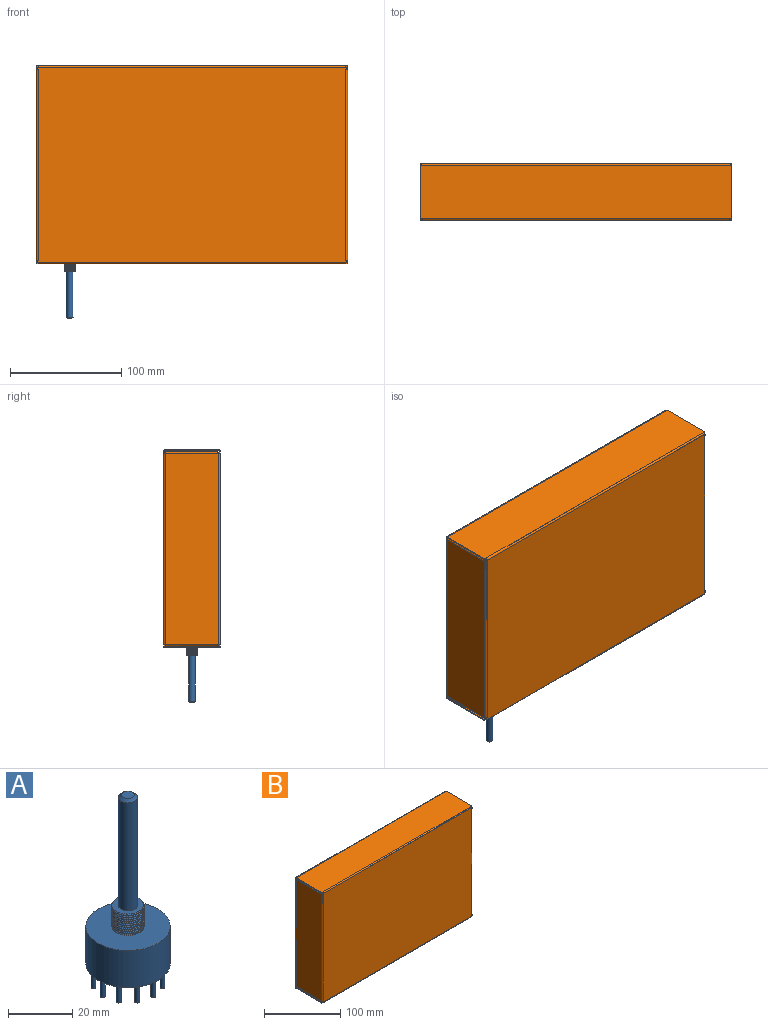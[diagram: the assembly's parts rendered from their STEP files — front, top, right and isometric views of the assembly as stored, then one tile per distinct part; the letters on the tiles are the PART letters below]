
ASSEMBLY  parts=2 mates=1
PART A: 35 faces, bbox 26.4x26.4x71.3 mm
  f0: cylinder r=5mm len=10mm, axis (0,0,-1), area 117.9mm2, adj f1,f2,f3,f4,f8
  f1: plane 10.15x9.87mm, normal (0,0,1), area 47.4mm2, adj f0,f3,f4,f5
  f2: plane 0.4x0.3mm, normal (-0.87,-0.5,0), area 0.1mm2, adj f0,f3,f4
  f3: bspline ~11.55x10mm, area 128mm2, adj f0,f1,f2,f4
  f4: bspline ~11.55x10mm, area 124.5mm2, adj f0,f1,f2,f3
  f5: cylinder r=3mm len=41mm, axis (0,0,-1), area 772.8mm2, adj f1,f7
  f6: plane 4x4mm, normal (0,0,1), area 12.6mm2, adj f7
  f7: cone r=2mm half-angle=45deg, axis (0,0,-1), area 22.2mm2, adj f5,f6
  f8: plane 26.2x26.2mm, normal (0,0,1), area 460.6mm2, adj f0,f9
  f9: cylinder r=13.1mm len=26.2mm, axis (0,0,1), area 1160.6mm2, adj f8,f10
  f10: plane 26.2x26.2mm, normal (0,0,-1), area 517.9mm2, adj f9,f11,f13,f15,f17,f19,f21,f23
  f11: cylinder r=0.75mm len=7mm, axis (0,0,1), area 33mm2, adj f10,f12
  f12: plane 1.5x1.5mm, normal (0,0,-1), area 1.8mm2, adj f11
  f13: cylinder r=0.75mm len=7mm, axis (0,0,1), area 33mm2, adj f10,f14
  f14: plane 1.5x1.5mm, normal (0,0,-1), area 1.8mm2, adj f13
  f15: cylinder r=0.75mm len=7mm, axis (0,0,1), area 33mm2, adj f10,f16
  f16: plane 1.5x1.5mm, normal (0,0,-1), area 1.8mm2, adj f15
  f17: cylinder r=0.75mm len=7mm, axis (0,0,1), area 33mm2, adj f10,f18
  f18: plane 1.5x1.5mm, normal (0,0,-1), area 1.8mm2, adj f17
  f19: cylinder r=0.75mm len=7mm, axis (0,0,1), area 33mm2, adj f10,f20
  f20: plane 1.5x1.5mm, normal (0,0,-1), area 1.8mm2, adj f19
  f21: cylinder r=0.75mm len=7mm, axis (0,0,1), area 33mm2, adj f10,f22
  f22: plane 1.5x1.5mm, normal (0,0,-1), area 1.8mm2, adj f21
  f23: cylinder r=0.75mm len=7mm, axis (0,0,1), area 33mm2, adj f10,f24
  f24: plane 1.5x1.5mm, normal (0,0,-1), area 1.8mm2, adj f23
  f25: cylinder r=0.75mm len=7mm, axis (0,0,1), area 33mm2, adj f10,f26
  f26: plane 1.5x1.5mm, normal (0,0,-1), area 1.8mm2, adj f25
  f27: cylinder r=0.75mm len=7mm, axis (0,0,1), area 33mm2, adj f10,f28
  f28: plane 1.5x1.5mm, normal (0,0,-1), area 1.8mm2, adj f27
  f29: cylinder r=0.75mm len=7mm, axis (0,0,1), area 33mm2, adj f10,f30
  f30: plane 1.5x1.5mm, normal (0,0,-1), area 1.8mm2, adj f29
  f31: cylinder r=0.75mm len=7mm, axis (0,0,1), area 33mm2, adj f10,f32
  f32: plane 1.5x1.5mm, normal (0,0,-1), area 1.8mm2, adj f31
  f33: cylinder r=0.75mm len=7mm, axis (0,0,1), area 33mm2, adj f10,f34
  f34: plane 1.5x1.5mm, normal (0,0,-1), area 1.8mm2, adj f33
PART B: 122 faces, bbox 279.4x50.8x177.8 mm
  f0: bspline ~1.52x1.52mm, area 2.3mm2, adj f1,f49,f53,f100
  f1: cylinder r=1.52mm len=47.75mm, axis (0,1,0), area 112.5mm2, adj f0,f50,f51,f55
  f2: plane 1.52x1.52mm, normal (0,0,-1), area 1.6mm2, adj f3,f4,f39,f43
  f3: cylinder r=0.51mm len=171.7mm, axis (0,0,-1), area 137mm2, adj f2,f45,f54,f57
  f4: cylinder r=1.52mm len=171.7mm, axis (0,0,-1), area 411mm2, adj f2,f46,f54,f55
  f5: cylinder r=1.52mm len=47.75mm, axis (0,-1,0), area 112.5mm2, adj f6,f39,f40,f55
  f6: bspline ~1.52x1.52mm, area 2.3mm2, adj f5,f41,f56,f99
  f7: cylinder r=0.51mm len=47.75mm, axis (0,1,0), area 37.5mm2, adj f8,f35,f36,f62
  f8: bspline ~1.52x1.52mm, area 2.3mm2, adj f7,f33,f58,f98
  f9: plane 8.79x8.79mm, normal (-0.71,0,0.71), area 12.6mm2, adj f11,f44,f45,f46
  f10: plane 8.79x8.79mm, normal (-0.71,0,-0.71), area 12.6mm2, adj f11,f43,f45,f46
  f11: plane 154.94x1.02mm, normal (-1,0,0), area 157.4mm2, adj f9,f10,f45,f46
  f12: plane 1.52x1.02mm, normal (0,-1,0), area 1.5mm2, adj f13,f16,f18,f82
  f13: plane 47.75x1.02mm, normal (-1,0,0), area 48.5mm2, adj f12,f16,f18,f107
  f14: plane 1.52x1.02mm, normal (0,-1,0), area 1.5mm2, adj f16,f17,f18,f79
  f15: plane 29.06x1.02mm, normal (1,0,0), area 29.5mm2, adj f19,f21,f22,f23
  f16: plane 279.4x47.75mm, normal (0,0,-1), area 12457.3mm2, adj f12,f13,f14,f17,f90,f108,f114,f115
  f17: plane 47.75x1.02mm, normal (1,0,0), area 48.5mm2, adj f14,f16,f18,f106
  f18: plane 279.4x47.75mm, normal (0,0,1), area 12457.3mm2, adj f12,f13,f14,f17,f91,f109,f114,f115
  f19: plane 8.38x8.38mm, normal (0.71,0.71,0), area 12mm2, adj f15,f20,f21,f23
  f20: plane 1.93x1.52mm, normal (0,1,0), area 2mm2, adj f19,f21,f23,f93,f94,f95
  f21: plane 46.23x8.79mm, normal (0,0,1), area 332.5mm2, adj f15,f19,f20,f22,f93
  f22: plane 8.79x8.79mm, normal (0.71,-0.71,0), area 12.6mm2, adj f15,f21,f23,f92
  f23: plane 46.23x8.79mm, normal (0,0,-1), area 332.5mm2, adj f15,f19,f20,f22,f94
  f24: plane 1.02x0.41mm, normal (-1,0,0), area 0.4mm2, adj f26,f29,f30,f59
  f25: plane 154.94x1.02mm, normal (1,0,0), area 157.4mm2, adj f26,f27,f29,f30
  f26: plane 8.79x8.79mm, normal (0.71,0,-0.71), area 12.6mm2, adj f24,f25,f29,f30
  f27: plane 8.79x8.79mm, normal (0.71,0,0.71), area 12.6mm2, adj f25,f28,f29,f30
  f28: plane 1.02x0.41mm, normal (-1,0,0), area 0.4mm2, adj f27,f29,f30,f95
  f29: plane 172.52x8.79mm, normal (0,-1,0), area 1425.3mm2, adj f24,f25,f26,f27,f28,f97,f112,f113
  f30: plane 172.52x8.79mm, normal (0,1,0), area 1425.3mm2, adj f24,f25,f26,f27,f28,f96,f112,f113
  f31: plane 8.38x8.38mm, normal (0.71,0.71,0), area 12mm2, adj f32,f34,f35,f36
  f32: plane 29.06x1.02mm, normal (1,0,0), area 29.5mm2, adj f31,f33,f34,f36
  f33: plane 8.79x8.79mm, normal (0.71,-0.71,0), area 12.6mm2, adj f8,f32,f34,f36
  f34: plane 46.23x8.79mm, normal (0,0,-1), area 332.5mm2, adj f31,f32,f33,f35,f98
  f35: plane 1.93x1.52mm, normal (0,1,0), area 2mm2, adj f7,f31,f34,f36,f59,f98
  f36: plane 46.23x8.79mm, normal (0,0,1), area 332.5mm2, adj f7,f31,f32,f33,f35
  f37: plane 29.06x1.02mm, normal (-1,0,0), area 29.5mm2, adj f38,f40,f41,f42
  f38: plane 8.38x8.38mm, normal (-0.71,0.71,0), area 12mm2, adj f37,f39,f40,f42
  f39: plane 1.93x1.52mm, normal (0,1,0), area 2mm2, adj f2,f5,f38,f40,f42,f99
  f40: plane 46.23x8.79mm, normal (0,0,-1), area 332.5mm2, adj f5,f37,f38,f39,f41
  f41: plane 8.79x8.79mm, normal (-0.71,-0.71,0), area 12.6mm2, adj f6,f37,f40,f42
  f42: plane 46.23x8.79mm, normal (0,0,1), area 332.5mm2, adj f37,f38,f39,f41,f99
  f43: plane 1.02x0.41mm, normal (1,0,0), area 0.4mm2, adj f2,f10,f45,f46
  f44: plane 1.02x0.41mm, normal (1,0,0), area 0.4mm2, adj f9,f45,f46,f54
  f45: plane 172.52x8.79mm, normal (0,-1,0), area 1425.3mm2, adj f3,f9,f10,f11,f43,f44,f110,f111
  f46: plane 172.52x8.79mm, normal (0,1,0), area 1425.3mm2, adj f4,f9,f10,f11,f43,f44,f110,f111
  f47: plane 8.38x8.38mm, normal (-0.71,0.71,0), area 12mm2, adj f48,f50,f51,f52
  f48: plane 29.06x1.02mm, normal (-1,0,0), area 29.5mm2, adj f47,f49,f50,f52
  f49: plane 8.79x8.79mm, normal (-0.71,-0.71,0), area 12.6mm2, adj f0,f48,f50,f52
  f50: plane 46.23x8.79mm, normal (0,0,1), area 332.5mm2, adj f1,f47,f48,f49,f51
  f51: plane 1.93x1.52mm, normal (0,1,0), area 2mm2, adj f1,f47,f50,f52,f54,f100
  f52: plane 46.23x8.79mm, normal (0,0,-1), area 332.5mm2, adj f47,f48,f49,f51,f100
  f53: plane 1.52x1.52mm, normal (0,0,1), area 1.6mm2, adj f0,f80,f84,f85
  f54: plane 1.52x1.52mm, normal (0,0,1), area 1.6mm2, adj f3,f4,f44,f51
  f55: plane 171.7x47.75mm, normal (1,0,0), area 8199.2mm2, adj f1,f4,f5,f84
  f56: plane 1.52x1.52mm, normal (0,0,-1), area 1.6mm2, adj f6,f79,f84,f85
  f57: plane 171.7x47.75mm, normal (-1,0,0), area 8199.2mm2, adj f3,f85,f99,f100
  f58: plane 1.52x1.52mm, normal (0,0,-1), area 1.6mm2, adj f8,f82,f86,f87
  f59: plane 1.52x1.52mm, normal (0,0,-1), area 1.6mm2, adj f24,f35,f96,f97
  f60: plane 171.7x47.75mm, normal (-1,0,0), area 8199.2mm2, adj f86,f93,f96,f98
  f61: plane 1.52x1.52mm, normal (0,0,1), area 1.6mm2, adj f78,f86,f87,f92
  f62: plane 171.7x47.75mm, normal (1,0,0), area 8199.2mm2, adj f7,f87,f94,f97
  f63: plane 1.52x1.02mm, normal (0,-1,0), area 1.5mm2, adj f65,f67,f68,f80
  f64: plane 47.75x1.02mm, normal (-1,0,0), area 48.5mm2, adj f66,f67,f68,f74
  f65: plane 47.75x1.02mm, normal (1,0,0), area 48.5mm2, adj f63,f67,f68,f75
  f66: plane 1.52x1.02mm, normal (0,-1,0), area 1.5mm2, adj f64,f67,f68,f78
  f67: plane 279.4x47.75mm, normal (0,0,-1), area 13341.9mm2, adj f63,f64,f65,f66,f77,f89
  f68: plane 279.4x47.75mm, normal (0,0,1), area 13341.9mm2, adj f63,f64,f65,f66,f76,f88
  f69: plane 258.78x1.02mm, normal (0,0,-1), area 262.9mm2, adj f70,f71,f72,f73
  f70: plane 8.79x8.79mm, normal (-0.71,0,-0.71), area 12.6mm2, adj f69,f71,f73,f74
  f71: plane 276.35x8.79mm, normal (0,1,0), area 2351.5mm2, adj f69,f70,f72,f76
  f72: plane 8.79x8.79mm, normal (0.71,0,-0.71), area 12.6mm2, adj f69,f71,f73,f75
  f73: plane 276.35x8.79mm, normal (0,-1,0), area 2351.5mm2, adj f69,f70,f72,f77
  f74: bspline ~1.52x1.52mm, area 2.3mm2, adj f64,f70,f76,f77
  f75: bspline ~1.52x1.52mm, area 2.3mm2, adj f65,f72,f76,f77
  f76: cylinder r=1.52mm len=279.4mm, axis (1,0,0), area 665.2mm2, adj f68,f71,f74,f75
  f77: cylinder r=0.51mm len=279.4mm, axis (1,0,0), area 221.7mm2, adj f67,f73,f74,f75
  f78: plane 3.05x1.52mm, normal (-1,0,0), area 3.2mm2, adj f61,f66,f81,f83,f88,f89
  f79: plane 3.05x1.52mm, normal (1,0,0), area 3.2mm2, adj f14,f56,f81,f83,f90,f91
  f80: plane 3.05x1.52mm, normal (1,0,0), area 3.2mm2, adj f53,f63,f81,f83,f88,f89
  f81: plane 276.35x174.75mm, normal (0,1,0), area 48293.1mm2, adj f78,f79,f80,f82,f85,f87,f89,f91
  f82: plane 3.05x1.52mm, normal (-1,0,0), area 3.2mm2, adj f12,f58,f81,f83,f90,f91
  f83: plane 276.35x174.75mm, normal (0,-1,0), area 48293.1mm2, adj f78,f79,f80,f82,f84,f86,f88,f90
  f84: cylinder r=1.52mm len=171.7mm, axis (0,0,-1), area 411mm2, adj f53,f55,f56,f83
  f85: cylinder r=0.51mm len=171.7mm, axis (0,0,-1), area 137mm2, adj f53,f56,f57,f81
  f86: cylinder r=1.52mm len=171.7mm, axis (0,0,1), area 411mm2, adj f58,f60,f61,f83
  f87: cylinder r=0.51mm len=171.7mm, axis (0,0,1), area 137mm2, adj f58,f61,f62,f81
  f88: cylinder r=1.52mm len=276.35mm, axis (1,0,0), area 661.6mm2, adj f68,f78,f80,f83
  f89: cylinder r=0.51mm len=276.35mm, axis (1,0,0), area 220.5mm2, adj f67,f78,f80,f81
  f90: cylinder r=1.52mm len=276.35mm, axis (-1,0,0), area 661.6mm2, adj f16,f79,f82,f83
  f91: cylinder r=0.51mm len=276.35mm, axis (-1,0,0), area 220.5mm2, adj f18,f79,f81,f82
  f92: bspline ~1.52x1.52mm, area 2.3mm2, adj f22,f61,f93,f94
  f93: cylinder r=1.52mm len=47.75mm, axis (0,-1,0), area 112.5mm2, adj f20,f21,f60,f92
  f94: cylinder r=0.51mm len=47.75mm, axis (0,-1,0), area 37.5mm2, adj f20,f23,f62,f92
  f95: plane 1.52x1.52mm, normal (0,0,1), area 1.6mm2, adj f20,f28,f96,f97
  f96: cylinder r=1.52mm len=171.7mm, axis (0,0,1), area 411mm2, adj f30,f59,f60,f95
  f97: cylinder r=0.51mm len=171.7mm, axis (0,0,1), area 137mm2, adj f29,f59,f62,f95
  f98: cylinder r=1.52mm len=47.75mm, axis (0,1,0), area 112.5mm2, adj f8,f34,f35,f60
  f99: cylinder r=0.51mm len=47.75mm, axis (0,-1,0), area 37.5mm2, adj f6,f39,f42,f57
  f100: cylinder r=0.51mm len=47.75mm, axis (0,1,0), area 37.5mm2, adj f0,f51,f52,f57
  f101: plane 258.78x1.02mm, normal (0,0,1), area 262.9mm2, adj f102,f103,f104,f105
  f102: plane 8.79x8.79mm, normal (0.71,0,0.71), area 12.6mm2, adj f101,f103,f105,f106
  f103: plane 276.35x8.79mm, normal (0,1,0), area 2351.5mm2, adj f101,f102,f104,f108
  f104: plane 8.79x8.79mm, normal (-0.71,0,0.71), area 12.6mm2, adj f101,f103,f105,f107
  f105: plane 276.35x8.79mm, normal (0,-1,0), area 2351.5mm2, adj f101,f102,f104,f109
  f106: bspline ~1.52x1.52mm, area 2.3mm2, adj f17,f102,f108,f109
  f107: bspline ~1.52x1.52mm, area 2.3mm2, adj f13,f104,f108,f109
  f108: cylinder r=1.52mm len=279.4mm, axis (-1,0,0), area 665.2mm2, adj f16,f103,f106,f107
  f109: cylinder r=0.51mm len=279.4mm, axis (-1,0,0), area 221.7mm2, adj f18,f105,f106,f107
  f110: cylinder r=1.47mm len=2.95mm, axis (0,-1,0), area 9.4mm2, adj f45,f46
  f111: cylinder r=1.47mm len=2.95mm, axis (0,-1,0), area 9.4mm2, adj f45,f46
  f112: cylinder r=1.47mm len=2.95mm, axis (0,-1,0), area 9.4mm2, adj f29,f30
  f113: cylinder r=1.47mm len=2.95mm, axis (0,-1,0), area 9.4mm2, adj f29,f30
  f114: cylinder r=9mm len=18mm, axis (0,0,-1), area 57.5mm2, adj f16,f18
  f115: cylinder r=5.1mm len=10.2mm, axis (0,0,-1), area 32.6mm2, adj f16,f18
  f116: cylinder r=1.6mm len=3.2mm, axis (0,0,-1), area 10.2mm2, adj f16,f18
  f117: cylinder r=9mm len=18mm, axis (0,0,-1), area 57.5mm2, adj f16,f18
  f118: cylinder r=4.5mm len=9mm, axis (0,0,-1), area 28.7mm2, adj f16,f18
  f119: cylinder r=4.5mm len=9mm, axis (0,0,-1), area 28.7mm2, adj f16,f18
  f120: cylinder r=4.5mm len=9mm, axis (0,0,-1), area 28.7mm2, adj f16,f18
  f121: cylinder r=5.5mm len=11mm, axis (0,0,-1), area 35.1mm2, adj f16,f18
PLACE A rot(axis=(0,1,0),180deg) t=(-109.7,-25.4,-87.88)mm
PLACE B at identity
MATE fastened A.f0 <-> B.f115  axis (0,0,-1) through (-109.7,-25.4,-87.88)mm
